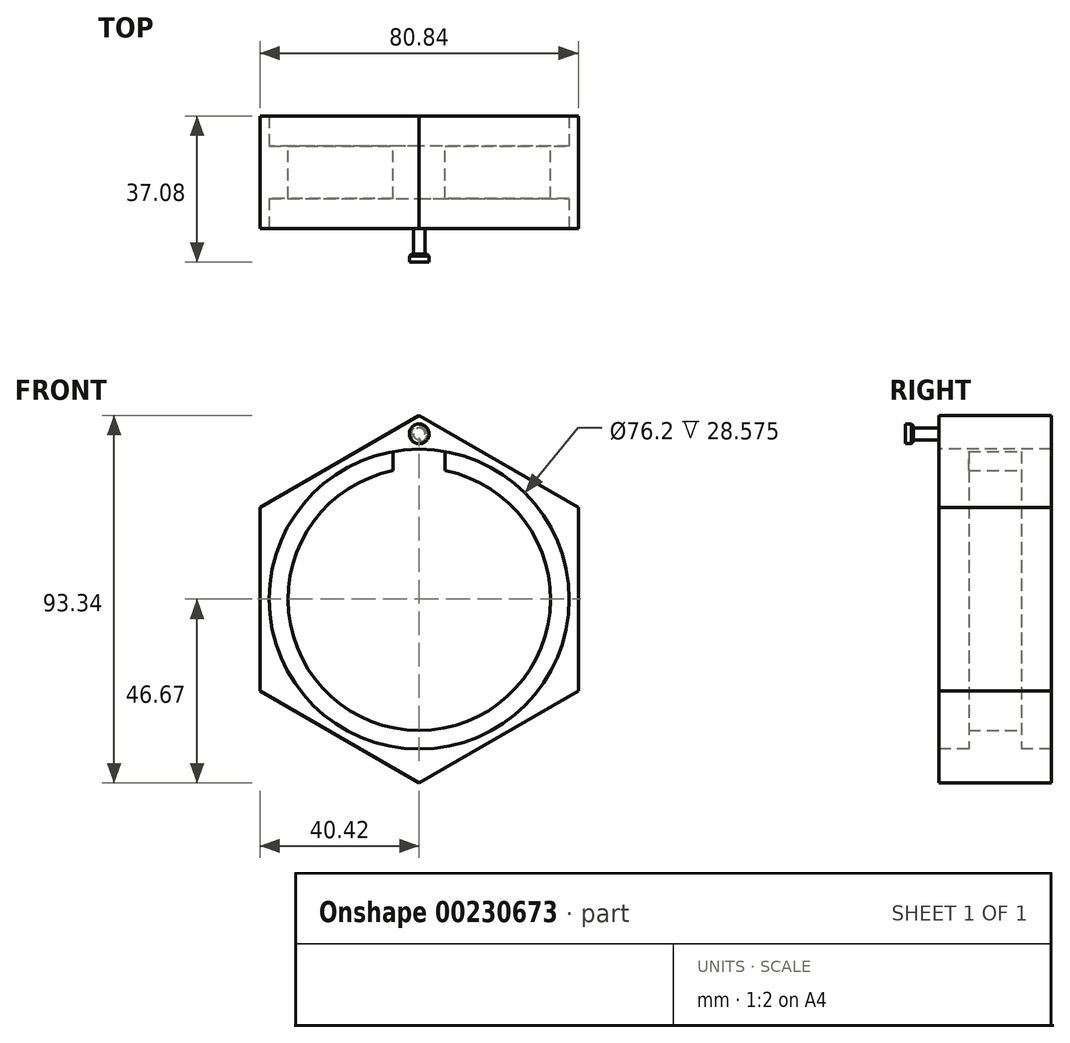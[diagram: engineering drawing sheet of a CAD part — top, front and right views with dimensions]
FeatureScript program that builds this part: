
annotation { "Feature Type Name" : "Feature", "Feature Type Description" : "" }
export const myFeature = defineFeature(function(context is Context, id is Id, definition is map)
    precondition{}
    {
        {
            var Q0;
            Q0=qCreatedBy(makeId("Front.planeOp"),FACE);
            var sketch = newSketch(context, id + "F0", { "sketchPlane" : qUnion([Q0])});
            skCircle(sketch, "E0.cCircle", {"center": v(0, 0) * mm, "radius": 62.23 * mm, "construction": true});
            skLineSegment(sketch, "E0.0", {"start": v(0, 62.23) * mm, "end": v(53.9, 31.12) * mm});
            skLineSegment(sketch, "E0.1", {"start": v(53.9, 31.12) * mm, "end": v(53.9, -31.11) * mm});
            skLineSegment(sketch, "E0.2", {"start": v(53.9, -31.11) * mm, "end": v(0, -62.23) * mm});
            skLineSegment(sketch, "E0.3", {"start": v(0, -62.23) * mm, "end": v(-53.9, -31.12) * mm});
            skLineSegment(sketch, "E0.4", {"start": v(-53.9, -31.12) * mm, "end": v(-53.9, 31.11) * mm});
            skLineSegment(sketch, "E0.5", {"start": v(-53.9, 31.11) * mm, "end": v(0, 62.23) * mm});
            skCircle(sketch, "E1", {"center": v(0, 0) * mm, "radius": 44.45 * mm});
            skSolve(sketch);
        }
        {
            var Q0;
            Q0=qSketchRegion(id+"F0",true);
            extrude(context, id + "F1", {"entities" : qUnion([Q0]), "depth" : 38.1 * mm});
        }
        {
            var Q0;
            Q0=makeQuery(id+"F1.opExtrude","CAP_FACE",FACE,{"disambiguationData":[OSD([sQuery(id+"F0.wireOp",EDGE,"E0.0"),sQuery(id+"F0.wireOp",EDGE,"E0.1"),sQuery(id+"F0.wireOp",EDGE,"E0.2"),sQuery(id+"F0.wireOp",EDGE,"E0.3"),sQuery(id+"F0.wireOp",EDGE,"E0.4"),sQuery(id+"F0.wireOp",EDGE,"E0.5"),sQuery(id+"F0.wireOp",EDGE,"E1")])],"isStart":false});
            var sketch = newSketch(context, id + "F2", { "sketchPlane" : qUnion([Q0])});
            skCircle(sketch, "E2", {"center": v(0, 0) * mm, "radius": 50.8 * mm});
            skSolve(sketch);
        }
        {
            var Q0;
            Q0=qSketchRegion(id+"F2",true);
            extrude(context, id + "F3", {"entities" : qUnion([Q0]), "operationType" : NewBodyOperationType.REMOVE, "oppositeDirection" : true, "depth" : 10.16 * mm});
        }
        {
            var Q0;
            Q0=makeQuery(id+"F1.opExtrude","CAP_FACE",FACE,{"disambiguationData":[OSD([sQuery(id+"F0.wireOp",EDGE,"E0.0"),sQuery(id+"F0.wireOp",EDGE,"E0.1"),sQuery(id+"F0.wireOp",EDGE,"E0.2"),sQuery(id+"F0.wireOp",EDGE,"E0.3"),sQuery(id+"F0.wireOp",EDGE,"E0.4"),sQuery(id+"F0.wireOp",EDGE,"E0.5"),sQuery(id+"F0.wireOp",EDGE,"E1")])],"isStart":true});
            var sketch = newSketch(context, id + "F4", { "sketchPlane" : qUnion([Q0])});
            skCircle(sketch, "E3", {"center": v(0, 0) * mm, "radius": 50.8 * mm});
            skSolve(sketch);
        }
        {
            var Q0;
            Q0=qSketchRegion(id+"F4",true);
            extrude(context, id + "F5", {"entities" : qUnion([Q0]), "operationType" : NewBodyOperationType.REMOVE, "oppositeDirection" : true, "depth" : 10.16 * mm});
        }
        {
            var Q0;
            Q0=makeQuery(id+"F5.boolean.opBoolean","COPY",FACE,{"derivedFrom":makeQuery(id+"F5.opExtrude","CAP_FACE",FACE,{"disambiguationData":[OSD([sQuery(id+"F4.wireOp",EDGE,"E3")])],"isStart":false})});
            var sketch = newSketch(context, id + "F6", { "sketchPlane" : qUnion([Q0])});
            skCircle(sketch, "E4", {"center": v(0, 0) * mm, "radius": 50.8 * mm});
            skCircle(sketch, "E5", {"center": v(0, 0) * mm, "radius": 44.45 * mm});
            skLineSegment(sketch, "E6", {"start": v(0, 0) * mm, "end": v(-8.82, 50.03) * mm});
            skLineSegment(sketch, "E7", {"start": v(0, 0) * mm, "end": v(8.82, 50.03) * mm});
            skLineSegment(sketch, "E8", {"start": v(-8.82, 50.03) * mm, "end": v(-8.82, 0) * mm});
            skLineSegment(sketch, "E9", {"start": v(8.82, 50.03) * mm, "end": v(8.82, 0) * mm});
            skSolve(sketch);
        }
        {
            var Q0;
            {var subQ0=sQuery(id+"F6.wireOp",EDGE,"E6");var subQ5=sQuery(id+"F6.wireOp",EDGE,"E5");var subQ6=makeQuery(id+"F6.imprint","INTERSECT",VERTEX,{"derivedFrom":[subQ5,subQ0]});Q0=makeQuery(id+"F6.imprint","IMPRINT",FACE,{"disambiguationData":[TD([[makeQuery(id+"F6.imprint","IMPRINT",EDGE,{"disambiguationData":[TD([[subQ6,1.0]])],"derivedFrom":subQ5}),-1.0]])]});}
            var Q1;
            {var subQ0=sQuery(id+"F6.wireOp",EDGE,"E8");var subQ1=sQuery(id+"F6.wireOp",EDGE,"E5");var subQ2=makeQuery(id+"F6.imprint","INTERSECT",VERTEX,{"derivedFrom":[subQ1,subQ0]});Q1=makeQuery(id+"F6.imprint","IMPRINT",FACE,{"disambiguationData":[TD([[makeQuery(id+"F6.imprint","IMPRINT",EDGE,{"disambiguationData":[TD([[subQ2,1.0]])],"derivedFrom":subQ1}),-1.0]])]});}
            var Q2;
            {var subQ0=sQuery(id+"F6.wireOp",EDGE,"E9");var subQ1=sQuery(id+"F6.wireOp",EDGE,"E5");var subQ2=makeQuery(id+"F6.imprint","INTERSECT",VERTEX,{"derivedFrom":[subQ1,subQ0]});Q2=makeQuery(id+"F6.imprint","IMPRINT",FACE,{"disambiguationData":[TD([[makeQuery(id+"F6.imprint","IMPRINT",EDGE,{"disambiguationData":[TD([[subQ2,-1.0]])],"derivedFrom":subQ1}),-1.0]])]});}
            extrude(context, id + "F7", {"entities" : qUnion([Q0, Q1, Q2]), "operationType" : NewBodyOperationType.REMOVE, "oppositeDirection" : true, "depth" : 25.4 * mm});
        }
        {
            var Q0;
            Q0=makeQuery(id+"F1.opExtrude","SWEPT_BODY",BODY,{"disambiguationData":[OSD([sQuery(id+"F0.wireOp",EDGE,"E0.0"),sQuery(id+"F0.wireOp",EDGE,"E0.1"),sQuery(id+"F0.wireOp",EDGE,"E0.2"),sQuery(id+"F0.wireOp",EDGE,"E0.3"),sQuery(id+"F0.wireOp",EDGE,"E0.4"),sQuery(id+"F0.wireOp",EDGE,"E0.5"),sQuery(id+"F0.wireOp",EDGE,"E1")])]});
            var Q1;
            Q1=sQuery(id+"F0.wireOp",VERTEX,"E0.cCircle.center");
            transform(context, id + "F8", {"entities" : qUnion([Q0]), "transformType" : TransformType.SCALE_UNIFORMLY, "scale" : .75, "scalePoint" : qUnion([Q1]), "makeCopy" : false});
        }
        {
            var Q0;
            Q0=makeQuery(id+"F1.opExtrude","CAP_FACE",FACE,{"disambiguationData":[OSD([sQuery(id+"F0.wireOp",EDGE,"E0.0"),sQuery(id+"F0.wireOp",EDGE,"E0.1"),sQuery(id+"F0.wireOp",EDGE,"E0.2"),sQuery(id+"F0.wireOp",EDGE,"E0.3"),sQuery(id+"F0.wireOp",EDGE,"E0.4"),sQuery(id+"F0.wireOp",EDGE,"E0.5"),sQuery(id+"F0.wireOp",EDGE,"E1")])],"isStart":false});
            var sketch = newSketch(context, id + "F9", { "sketchPlane" : qUnion([Q0])});
            skCircle(sketch, "E10", {"center": v(0, 42) * mm, "radius": 1.5 * mm});
            skSolve(sketch);
        }
        {
            var Q0;
            Q0 = qSketchRegion(id + "F9", true);
            extrude(context, id + "F10", {"entities" : qUnion([Q0]), "operationType" : NewBodyOperationType.ADD, "depth" : 6.5 * mm});
        }
        {
            var Q0;
            Q0=makeQuery(id+"F10.opExtrude","CAP_FACE",FACE,{"disambiguationData":[OSD([sQuery(id+"F9.wireOp",EDGE,"E10")])],"isStart":false});
            var sketch = newSketch(context, id + "F11", { "sketchPlane" : qUnion([Q0])});
            skCircle(sketch, "E11", {"center": v(0, 42) * mm, "radius": 2.5 * mm});
            skSolve(sketch);
        }
        {
            var Q0;
            Q0 = qSketchRegion(id + "F11", true);
            extrude(context, id + "F12", {"entities" : qUnion([Q0]), "operationType" : NewBodyOperationType.ADD, "depth" : 2 * mm});
        }
        {
            var Q0;
            Q0=makeQuery(id+"F12.opExtrude","CAP_EDGE",EDGE,{"disambiguationData":[OSD([sQuery(id+"F11.wireOp",EDGE,"E11")])],"isStart":true});
            chamfer(context, id + "F13", {"entities" : qUnion([Q0]), "width" : .5 * mm, "tangentPropagation" : true});
        }
    });
